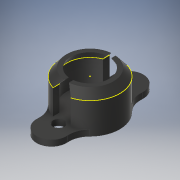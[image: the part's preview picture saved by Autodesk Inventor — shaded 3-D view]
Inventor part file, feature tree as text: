
AUTODESK INVENTOR PART (.ipt)
format: ipt  version: 2018 (Build 220112000, 112)  size: 213,504 bytes
history: native  units: in
note: dims shown in document units (in); Inventor stores cm internally (conversion verified against a paired STEP export)
features: sketch x6, extrude x2, loft x2, projected_geometry x2, other x2, plane x1, hole x1
ambient origin geometry x8: Origin, YZ Plane, XZ Plane, XY Plane, X Axis, Y Axis, Z Axis, Center Point
bodies: Solid1 (feature_tree)
feature tree (16):
  extrude  "Extrusion1"  Depth=0.25in
  extrude  "Extrusion2"  Depth=0.35in
  sketch  "Sketch3"  dims[d6=0.65in d7=0.05in d8=0.0in]
  plane  "Work Plane1"
  sketch  "Sketch4"  dims[d9=0.5in d10=0.395in]
  sketch  "Sketch5"  dims[d11=0.15in d12=0.2125in d13=0.0in]
  loft  "Loft1"
  loft  "Loft2"
  hole  "Hole1"  [1 undecoded]
  sketch  "Sketch1"  dims[d0=0.5in d2=0.25in]
  sketch  "Sketch2"  dims[d4=0.25in d5=0.35in]
  projected_geometry  "Projected Loop1"
  projected_geometry  "Projected Loop2"
  other  "Edges1"
  other  "Edges2"
  sketch  "Sketch6"  dims[d14=0.0625in d15=0.325in d16=0.395in d18=0.0in d19=90.0deg d20=0.0in d21=90.0deg d22=0.0in d23=90.0deg d24=0.0in d25=90.0deg d26=0.53in d27=0.096in d28=0.75in d29=0.172in d30=0.25in d31=0.5635in d32=1.0in d33=0.8108in d34=0.1975in d35=0.25in d36=0.1975in d37=0.25in]
note: 1 required parameter value undecoded (feature->parameter linkage not recoverable at this tier; creation-order binding heuristic only, values carry confidence <= 0.55)
